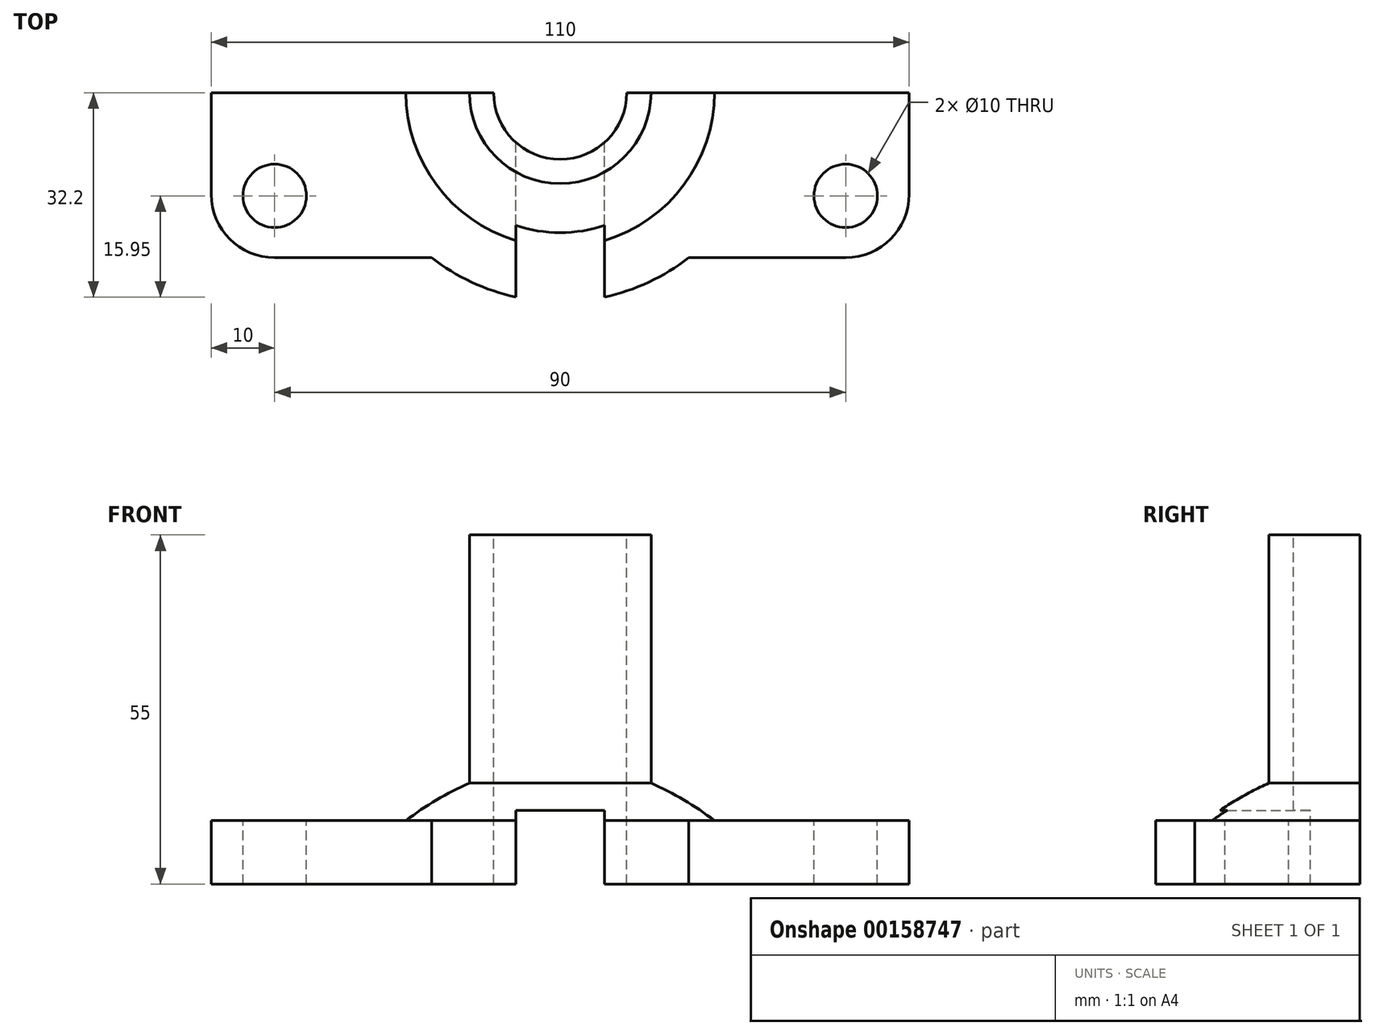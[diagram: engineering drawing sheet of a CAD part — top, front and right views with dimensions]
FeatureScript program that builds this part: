
annotation { "Feature Type Name" : "Feature", "Feature Type Description" : "" }
export const myFeature = defineFeature(function(context is Context, id is Id, definition is map)
    precondition{}
    {
        {
            var Q0;
            Q0=qCreatedBy(makeId("Top.planeOp"),FACE);
            var sketch = newSketch(context, id + "F0", { "sketchPlane" : qUnion([Q0])});
            skLineSegment(sketch, "E0.bottom", {"start": v(-55, 0) * mm, "end": v(55, 0) * mm});
            skLineSegment(sketch, "E0.top", {"start": v(-55, -26) * mm, "end": v(55, -26) * mm});
            skLineSegment(sketch, "E0.left", {"start": v(-55, 0) * mm, "end": v(-55, -26) * mm});
            skLineSegment(sketch, "E0.right", {"start": v(55, 0) * mm, "end": v(55, -26) * mm});
            skArc(sketch, "E1", {"start": v(-32.95, 0) * mm, "mid": v(0, -32.95) * mm, "end": v(32.95, 0) * mm});
            skSolve(sketch);
        }
        {
            var Q0;
            Q0 = qSketchRegion(id + "F0", true);
            extrude(context, id + "F1", {"entities" : qUnion([Q0]), "oppositeDirection" : true, "depth" : 10 * mm});
        }
        {
            var Q0;
            Q0=makeQuery(id+"F1.opExtrude","SWEPT_EDGE",EDGE,{"disambiguationData":[OSD([sQuery(id+"F0.wireOp",EDGE,"E0.top"),sQuery(id+"F0.wireOp",EDGE,"E0.left")])]});
            var Q1;
            Q1=makeQuery(id+"F1.opExtrude","SWEPT_EDGE",EDGE,{"disambiguationData":[OSD([sQuery(id+"F0.wireOp",EDGE,"E0.top"),sQuery(id+"F0.wireOp",EDGE,"E0.right")])]});
            fillet(context, id + "F2", {"entities" : qUnion([Q0, Q1]), "radius" : 10 * mm, "tangentPropagation" : true, "allowEdgeOverflow" : false});
        }
        {
            var Q0;
            Q0=qCreatedBy(makeId("Top.planeOp"),FACE);
            var sketch = newSketch(context, id + "F3", { "sketchPlane" : qUnion([Q0])});
            skCircle(sketch, "E2", {"center": v(-45, -16.25) * mm, "radius": 5 * mm});
            skCircle(sketch, "E3.MirrorC", {"center": v(45, -16.25) * mm, "radius": 5 * mm});
            skSolve(sketch);
        }
        {
            var Q0;
            Q0 = qSketchRegion(id + "F3", true);
            extrude(context, id + "F4", {"entities" : qUnion([Q0]), "operationType" : NewBodyOperationType.REMOVE, "oppositeDirection" : true, "depth" : 25 * mm});
        }
        {
            var Q0;
            Q0=qCreatedBy(makeId("Front.planeOp"),FACE);
            var sketch = newSketch(context, id + "F5", { "sketchPlane" : qUnion([Q0])});
            skLineSegment(sketch, "E4", {"start": v(0, 0) * mm, "end": v(24.32, 0) * mm});
            skLineSegment(sketch, "E5", {"start": v(0, 0) * mm, "end": v(0, 9.83) * mm});
            skArc(sketch, "E6", {"start": v(24.32, 0) * mm, "mid": v(12.81, 6.54) * mm, "end": v(0, 9.83) * mm});
            skSolve(sketch);
        }
        {
            var Q0;
            Q0=makeQuery(id+"F5.imprint","IMPRINT",FACE,{"disambiguationData":[TD([[makeQuery(id+"F5.imprint","IMPRINT",EDGE,{"derivedFrom":sQuery(id+"F5.wireOp",EDGE,"E4")}),1.0]])]});
            var Q1;
            Q1=sQuery(id+"F5.wireOp",EDGE,"E5");
            revolve(context, id + "F6", {"operationType" : NewBodyOperationType.ADD, "entities" : qUnion([Q0]), "axis" : qUnion([Q1]), "revolveType" : RevolveType.ONE_DIRECTION, "oppositeDirection" : true, "angle" : 180 * degree});
        }
        {
            var Q0;
            Q0=qCreatedBy(makeId("Top.planeOp"),FACE);
            var sketch = newSketch(context, id + "F7", { "sketchPlane" : qUnion([Q0])});
            skArc(sketch, "E7", {"start": v(14.32, 0) * mm, "mid": v(0, -14.32) * mm, "end": v(-14.32, 0) * mm});
            skLineSegment(sketch, "E8", {"start": v(-14.32, 0) * mm, "end": v(14.32, 0) * mm});
            skSolve(sketch);
        }
        {
            var Q0;
            Q0 = qSketchRegion(id + "F7", true);
            extrude(context, id + "F8", {"entities" : qUnion([Q0]), "operationType" : NewBodyOperationType.ADD, "depth" : 45 * mm});
        }
        {
            var Q0;
            Q0=qCreatedBy(makeId("Top.planeOp"),FACE);
            var sketch = newSketch(context, id + "F9", { "sketchPlane" : qUnion([Q0])});
            skCircle(sketch, "E9", {"center": v(0, 0) * mm, "radius": 10.5 * mm});
            skSolve(sketch);
        }
        {
            var Q0;
            Q0=makeQuery(id+"F9.imprint","IMPRINT",FACE,{"disambiguationData":[TD([[makeQuery(id+"F9.imprint","IMPRINT",EDGE,{"derivedFrom":sQuery(id+"F9.wireOp",EDGE,"E9")}),1.0]])]});
            extrude(context, id + "F10", {"entities" : qUnion([Q0]), "operationType" : NewBodyOperationType.REMOVE, "oppositeDirection" : true, "depth" : 50 * mm, "hasSecondDirection" : true, "secondDirectionOppositeDirection" : false, "secondDirectionDepth" : 50 * mm});
        }
        {
            var Q0;
            Q0=qCreatedBy(makeId("Front.planeOp"),FACE);
            var sketch = newSketch(context, id + "F11", { "sketchPlane" : qUnion([Q0])});
            skLineSegment(sketch, "E10.bottom", {"start": v(-7, 1.62) * mm, "end": v(7, 1.62) * mm});
            skLineSegment(sketch, "E10.top", {"start": v(-7, -23.67) * mm, "end": v(7, -23.67) * mm});
            skLineSegment(sketch, "E10.left", {"start": v(-7, 1.62) * mm, "end": v(-7, -23.67) * mm});
            skLineSegment(sketch, "E10.right", {"start": v(7, 1.62) * mm, "end": v(7, -23.67) * mm});
            skSolve(sketch);
        }
        {
            var Q0;
            Q0 = qSketchRegion(id + "F11", true);
            extrude(context, id + "F12", {"entities" : qUnion([Q0]), "operationType" : NewBodyOperationType.REMOVE, "depth" : 50 * mm});
        }
    });
